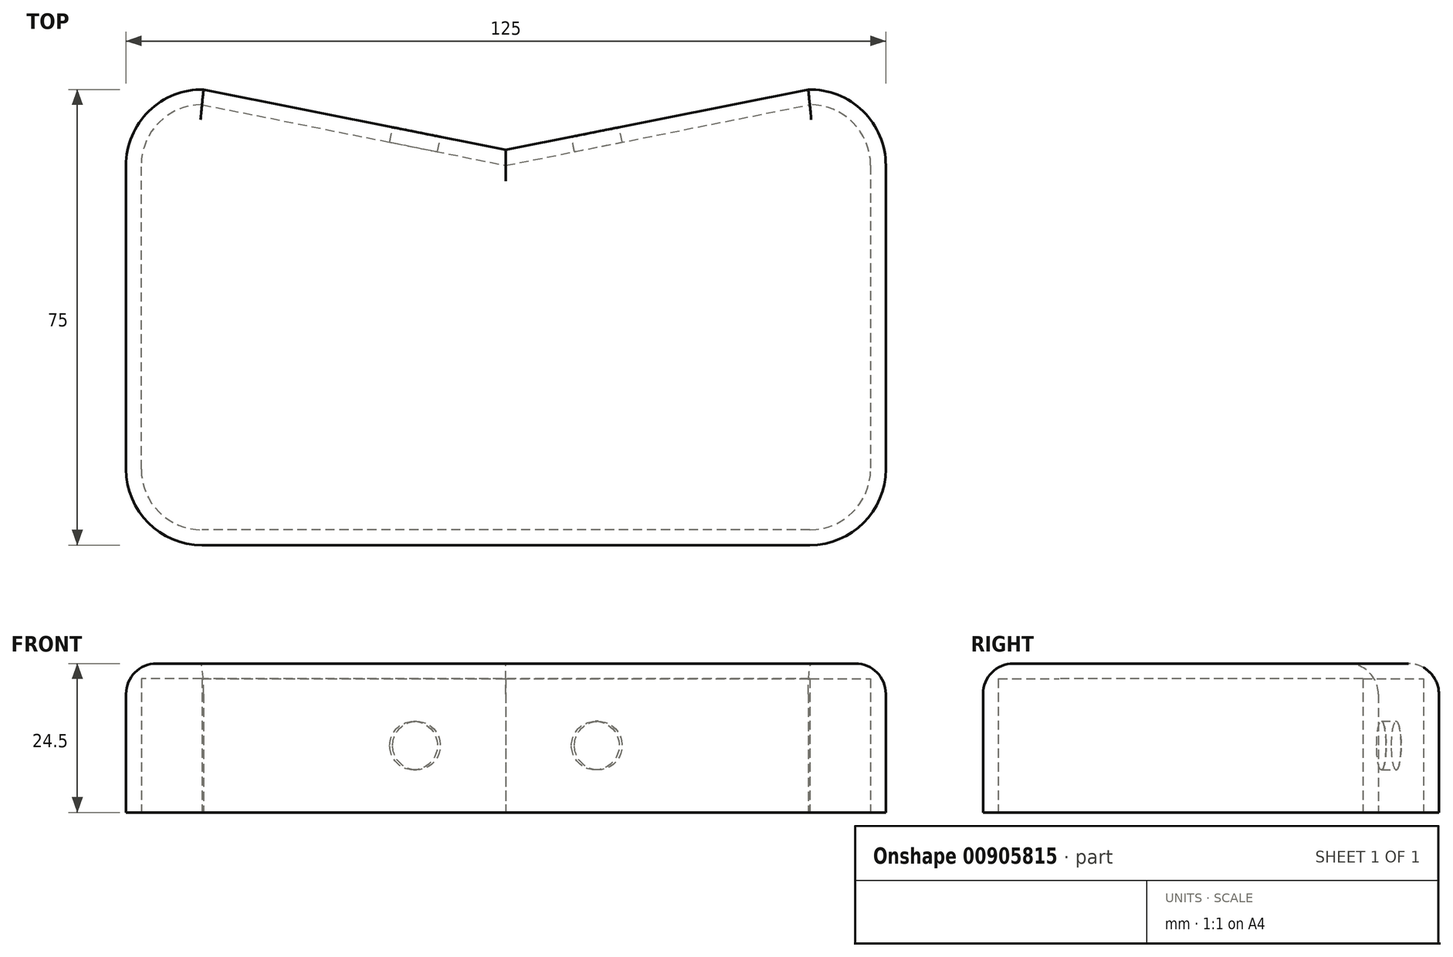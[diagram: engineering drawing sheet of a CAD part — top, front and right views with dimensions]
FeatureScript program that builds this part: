
annotation { "Feature Type Name" : "Feature", "Feature Type Description" : "" }
export const myFeature = defineFeature(function(context is Context, id is Id, definition is map)
    precondition{}
    {
        {
            var Q0;
            Q0=qCreatedBy(makeId("Top.planeOp"),FACE);
            var sketch = newSketch(context, id + "F0", { "sketchPlane" : qUnion([Q0])});
            skLineSegment(sketch, "E0", {"start": v(60, 15) * mm, "end": v(60, -35) * mm});
            skLineSegment(sketch, "E1", {"start": v(50, -45) * mm, "end": v(-50, -45) * mm});
            skLineSegment(sketch, "E2", {"start": v(-60, -35) * mm, "end": v(-60, 15) * mm});
            skPoint(sketch, "E3.visualSharp", {"position": v(-60, 25) * mm});
            skArc(sketch, "E3.filletArc", {"start": v(-50, 25) * mm, "mid": v(-57.07, 22.07) * mm, "end": v(-60, 15) * mm});
            skPoint(sketch, "E4.visualSharp", {"position": v(60, 25) * mm});
            skArc(sketch, "E4.filletArc", {"start": v(60, 15) * mm, "mid": v(57.07, 22.07) * mm, "end": v(50, 25) * mm});
            skPoint(sketch, "E5.visualSharp", {"position": v(60, -45) * mm});
            skArc(sketch, "E5.filletArc", {"start": v(50, -45) * mm, "mid": v(57.07, -42.07) * mm, "end": v(60, -35) * mm});
            skPoint(sketch, "E6.visualSharp", {"position": v(-60, -45) * mm});
            skArc(sketch, "E6.filletArc", {"start": v(-60, -35) * mm, "mid": v(-57.07, -42.07) * mm, "end": v(-50, -45) * mm});
            skPoint(sketch, "E7.endSnap0", {"position": v(0, 25) * mm});
            skLineSegment(sketch, "E8", {"start": v(0, 15) * mm, "end": v(50, 25) * mm});
            skLineSegment(sketch, "E9", {"start": v(-50, 25) * mm, "end": v(0, 15) * mm});
            skSolve(sketch);
        }
        {
            var Q0;
            Q0 = qSketchRegion(id + "F0", true);
            extrude(context, id + "F1", {"entities" : qUnion([Q0]), "depth" : 11 * mm, "offsetDistance" : 25 * mm});
        }
        {
            var Q0;
            Q0 = qSketchRegion(id + "F0", true);
            extrude(context, id + "F2", {"entities" : qUnion([Q0]), "operationType" : NewBodyOperationType.ADD, "depth" : -11 * mm, "offsetDistance" : 25 * mm});
        }
        {
            var Q0;
            Q0=makeQuery(id+"F2.opExtrude","CAP_FACE",FACE,{"disambiguationData":[OSD([sQuery(id+"F0.wireOp",EDGE,"E0"),sQuery(id+"F0.wireOp",EDGE,"E1"),sQuery(id+"F0.wireOp",EDGE,"E2"),sQuery(id+"F0.wireOp",EDGE,"E3.filletArc"),sQuery(id+"F0.wireOp",EDGE,"E4.filletArc"),sQuery(id+"F0.wireOp",EDGE,"E5.filletArc"),sQuery(id+"F0.wireOp",EDGE,"E6.filletArc"),sQuery(id+"F0.wireOp",EDGE,"E8"),sQuery(id+"F0.wireOp",EDGE,"E9")])],"isStart":false});
            shell(context, id + "F3", {"entities" : qUnion([Q0]), "thickness" : 2.5 * mm, "oppositeDirection" : true});
        }
        {
            var Q0;
            Q0=makeQuery(id+"F1.opExtrude","CAP_FACE",FACE,{"disambiguationData":[OSD([sQuery(id+"F0.wireOp",EDGE,"E0"),sQuery(id+"F0.wireOp",EDGE,"E1"),sQuery(id+"F0.wireOp",EDGE,"E2"),sQuery(id+"F0.wireOp",EDGE,"E3.filletArc"),sQuery(id+"F0.wireOp",EDGE,"E4.filletArc"),sQuery(id+"F0.wireOp",EDGE,"E5.filletArc"),sQuery(id+"F0.wireOp",EDGE,"E6.filletArc"),sQuery(id+"F0.wireOp",EDGE,"E8"),sQuery(id+"F0.wireOp",EDGE,"E9")])],"isStart":false});
            fillet(context, id + "F4", {"entities" : qUnion([Q0]), "radius" : 5 * mm, "tangentPropagation" : true, "allowEdgeOverflow" : false});
        }
        {
            var Q0;
            {var subQ0=sQuery(id+"F0.wireOp",EDGE,"E8");Q0=makeQuery(id+"F2.boolean.opBoolean","MERGE",FACE,{"derivedFrom":[makeQuery(id+"F1.opExtrude","SWEPT_FACE",FACE,{"disambiguationData":[OSD([subQ0])]}),makeQuery(id+"F2.opExtrude","SWEPT_FACE",FACE,{"disambiguationData":[OSD([subQ0])]})]});}
            var sketch = newSketch(context, id + "F5", { "sketchPlane" : qUnion([Q0])});
            skLineSegment(sketch, "E10", {"start": v(-3.44, 0) * mm, "end": v(-18.44, 0) * mm});
            skCircle(sketch, "E11", {"center": v(-18.44, 0) * mm, "radius": 4 * mm});
            skSolve(sketch);
        }
        {
            var Q0;
            {var subQ0=sQuery(id+"F0.wireOp",EDGE,"E9");Q0=makeQuery(id+"F2.boolean.opBoolean","MERGE",FACE,{"derivedFrom":[makeQuery(id+"F1.opExtrude","SWEPT_FACE",FACE,{"disambiguationData":[OSD([subQ0])]}),makeQuery(id+"F2.opExtrude","SWEPT_FACE",FACE,{"disambiguationData":[OSD([subQ0])]})]});}
            var sketch = newSketch(context, id + "F6", { "sketchPlane" : qUnion([Q0])});
            skLineSegment(sketch, "E12", {"start": v(3.44, 0) * mm, "end": v(18.44, 0) * mm});
            skCircle(sketch, "E13", {"center": v(18.44, 0) * mm, "radius": 4 * mm});
            skSolve(sketch);
        }
        {
            var Q0;
            Q0 = qSketchRegion(id + "F5", true);
            extrude(context, id + "F7", {"entities" : qUnion([Q0]), "operationType" : NewBodyOperationType.REMOVE, "oppositeDirection" : true, "depth" : 10 * mm, "offsetDistance" : 25 * mm});
        }
        {
            var Q0;
            Q0 = qSketchRegion(id + "F6", true);
            extrude(context, id + "F8", {"entities" : qUnion([Q0]), "operationType" : NewBodyOperationType.REMOVE, "oppositeDirection" : true, "depth" : 10 * mm, "offsetDistance" : 25 * mm});
        }
    });
